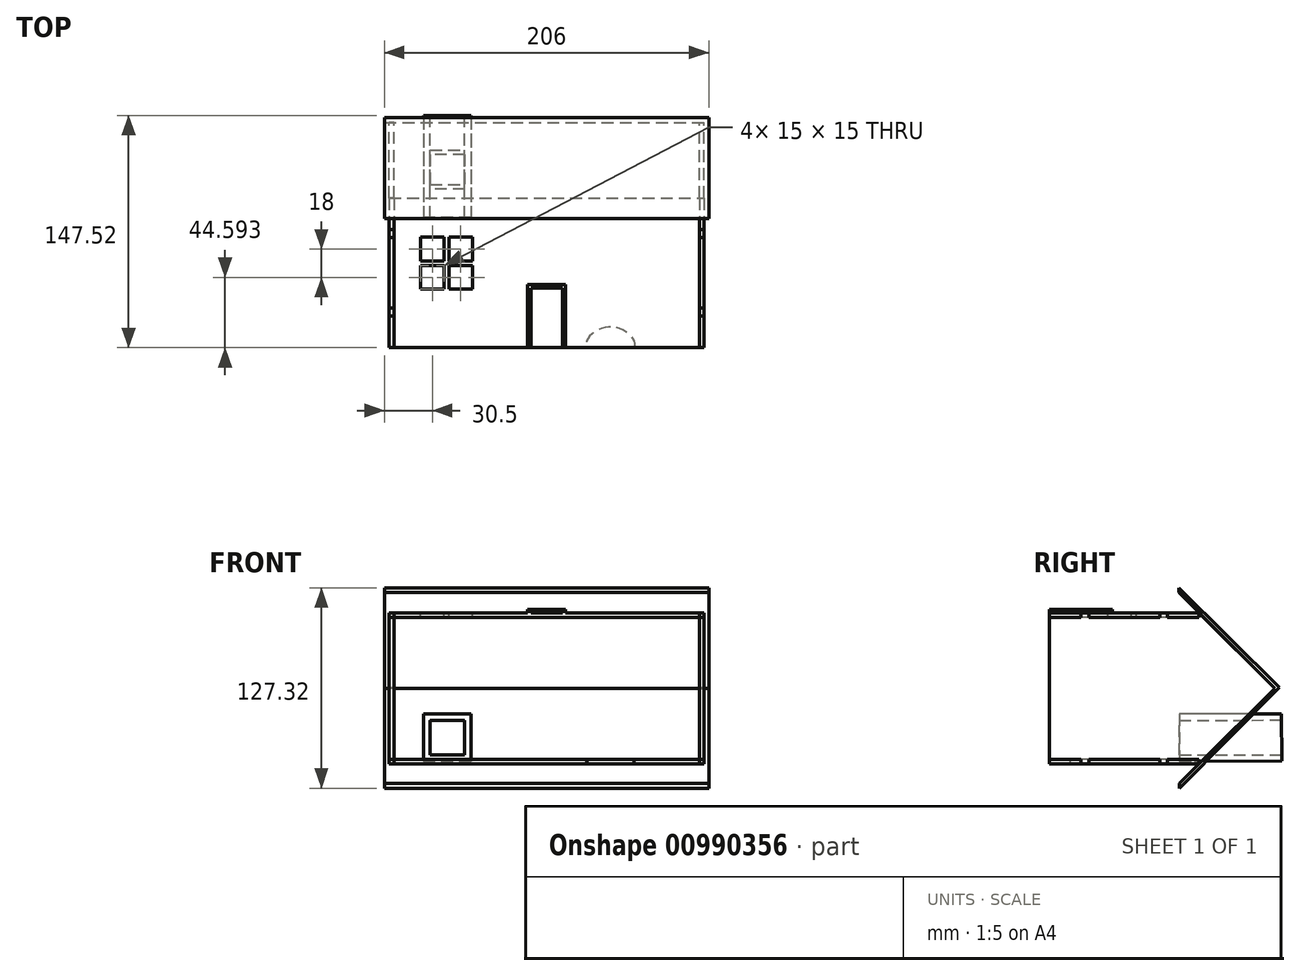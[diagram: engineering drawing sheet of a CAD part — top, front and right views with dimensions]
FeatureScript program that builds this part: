
annotation { "Feature Type Name" : "Feature", "Feature Type Description" : "" }
export const myFeature = defineFeature(function(context is Context, id is Id, definition is map)
    precondition{}
    {
        {
            var Q0;
            Q0=qCreatedBy(makeId("Top.planeOp"),FACE);
            var sketch = newSketch(context, id + "F0", { "sketchPlane" : qUnion([Q0])});
            skLineSegment(sketch, "E0.bottom", {"start": v(-100, 95) * mm, "end": v(100, 95) * mm});
            skLineSegment(sketch, "E0.top", {"start": v(-100, 0) * mm, "end": v(100, 0) * mm});
            skLineSegment(sketch, "E0.left", {"start": v(-100, 95) * mm, "end": v(-100, 0) * mm});
            skLineSegment(sketch, "E0.right", {"start": v(100, 95) * mm, "end": v(100, 0) * mm});
            skLineSegment(sketch, "E1.bottom", {"start": v(-100, 25) * mm, "end": v(-97, 25) * mm});
            skLineSegment(sketch, "E1.top", {"start": v(-100, 20) * mm, "end": v(-97, 20) * mm});
            skLineSegment(sketch, "E1.left", {"start": v(-100, 25) * mm, "end": v(-100, 20) * mm});
            skLineSegment(sketch, "E1.right", {"start": v(-97, 25) * mm, "end": v(-97, 20) * mm});
            skLineSegment(sketch, "E2.bottom", {"start": v(-100, 75) * mm, "end": v(-97, 75) * mm});
            skLineSegment(sketch, "E2.top", {"start": v(-100, 70) * mm, "end": v(-97, 70) * mm});
            skLineSegment(sketch, "E2.left", {"start": v(-100, 75) * mm, "end": v(-100, 70) * mm});
            skLineSegment(sketch, "E2.right", {"start": v(-97, 75) * mm, "end": v(-97, 70) * mm});
            skLineSegment(sketch, "E3.bottom", {"start": v(97, 25) * mm, "end": v(100, 25) * mm});
            skLineSegment(sketch, "E3.top", {"start": v(97, 20) * mm, "end": v(100, 20) * mm});
            skLineSegment(sketch, "E3.left", {"start": v(97, 25) * mm, "end": v(97, 20) * mm});
            skLineSegment(sketch, "E3.right", {"start": v(100, 25) * mm, "end": v(100, 20) * mm});
            skLineSegment(sketch, "E4.bottom", {"start": v(97, 75) * mm, "end": v(100, 75) * mm});
            skLineSegment(sketch, "E4.top", {"start": v(97, 70) * mm, "end": v(100, 70) * mm});
            skLineSegment(sketch, "E4.left", {"start": v(97, 75) * mm, "end": v(97, 70) * mm});
            skLineSegment(sketch, "E4.right", {"start": v(100, 75) * mm, "end": v(100, 70) * mm});
            skSolve(sketch);
        }
        {
            var Q0;
            Q0 = qSketchRegion(id + "F0", true);
            extrude(context, id + "F1", {"entities" : qUnion([Q0]), "depth" : 3 * mm, "offsetDistance" : 25 * mm});
        }
        {
            var Q0;
            Q0=makeQuery(id+"F1.opExtrude","CAP_FACE",FACE,{"disambiguationData":[OSD([sQuery(id+"F0.wireOp",EDGE,"E0.bottom"),sQuery(id+"F0.wireOp",EDGE,"E0.top"),sQuery(id+"F0.wireOp",EDGE,"E0.left"),sQuery(id+"F0.wireOp",EDGE,"E0.right"),sQuery(id+"F0.wireOp",EDGE,"E1.left"),sQuery(id+"F0.wireOp",EDGE,"E2.left"),sQuery(id+"F0.wireOp",EDGE,"E3.right"),sQuery(id+"F0.wireOp",EDGE,"E4.right")])],"isStart":false});
            var sketch = newSketch(context, id + "F2", { "sketchPlane" : qUnion([Q0])});
            skLineSegment(sketch, "E5.bottom", {"start": v(-100, 75) * mm, "end": v(-97, 75) * mm});
            skLineSegment(sketch, "E5.top", {"start": v(-100, 70) * mm, "end": v(-97, 70) * mm});
            skLineSegment(sketch, "E5.left", {"start": v(-100, 75) * mm, "end": v(-100, 70) * mm});
            skLineSegment(sketch, "E5.right", {"start": v(-97, 75) * mm, "end": v(-97, 70) * mm});
            skLineSegment(sketch, "E6.bottom", {"start": v(-100, 25) * mm, "end": v(-97, 25) * mm});
            skLineSegment(sketch, "E6.top", {"start": v(-100, 20) * mm, "end": v(-97, 20) * mm});
            skLineSegment(sketch, "E6.left", {"start": v(-100, 25) * mm, "end": v(-100, 20) * mm});
            skLineSegment(sketch, "E6.right", {"start": v(-97, 25) * mm, "end": v(-97, 20) * mm});
            skLineSegment(sketch, "E7.bottom", {"start": v(97, 75) * mm, "end": v(100, 75) * mm});
            skLineSegment(sketch, "E7.top", {"start": v(97, 70) * mm, "end": v(100, 70) * mm});
            skLineSegment(sketch, "E7.left", {"start": v(97, 75) * mm, "end": v(97, 70) * mm});
            skLineSegment(sketch, "E7.right", {"start": v(100, 75) * mm, "end": v(100, 70) * mm});
            skLineSegment(sketch, "E8.bottom", {"start": v(97, 25) * mm, "end": v(100, 25) * mm});
            skLineSegment(sketch, "E8.top", {"start": v(97, 20) * mm, "end": v(100, 20) * mm});
            skLineSegment(sketch, "E8.left", {"start": v(97, 25) * mm, "end": v(97, 20) * mm});
            skLineSegment(sketch, "E8.right", {"start": v(100, 25) * mm, "end": v(100, 20) * mm});
            skSolve(sketch);
        }
        {
            var Q0;
            Q0 = qSketchRegion(id + "F2", true);
            extrude(context, id + "F3", {"entities" : qUnion([Q0]), "operationType" : NewBodyOperationType.REMOVE, "oppositeDirection" : true, "depth" : 3 * mm, "offsetDistance" : 25 * mm});
        }
        {
            var Q0;
            Q0=makeQuery(id+"F1.opExtrude","CAP_FACE",FACE,{"disambiguationData":[OSD([sQuery(id+"F0.wireOp",EDGE,"E0.bottom"),sQuery(id+"F0.wireOp",EDGE,"E0.top"),sQuery(id+"F0.wireOp",EDGE,"E0.left"),sQuery(id+"F0.wireOp",EDGE,"E0.right"),sQuery(id+"F0.wireOp",EDGE,"E1.left"),sQuery(id+"F0.wireOp",EDGE,"E2.left"),sQuery(id+"F0.wireOp",EDGE,"E3.right"),sQuery(id+"F0.wireOp",EDGE,"E4.right")])],"isStart":true});
            cPlane(context, id + "F4", {"entities" : qUnion([Q0]), "cplaneType" : CPlaneType.OFFSET, "offset" : 45 * mm, "width" : 150 * mm, "height" : 150 * mm});
        }
        {
            var Q0;
            Q0=makeQuery(id+"F1.opExtrude","SWEPT_BODY",BODY,{"disambiguationData":[OSD([sQuery(id+"F0.wireOp",EDGE,"E0.bottom"),sQuery(id+"F0.wireOp",EDGE,"E0.top"),sQuery(id+"F0.wireOp",EDGE,"E0.left"),sQuery(id+"F0.wireOp",EDGE,"E0.right"),sQuery(id+"F0.wireOp",EDGE,"E1.left"),sQuery(id+"F0.wireOp",EDGE,"E2.left"),sQuery(id+"F0.wireOp",EDGE,"E3.right"),sQuery(id+"F0.wireOp",EDGE,"E4.right")])]});
            var Q1;
            Q1=qCreatedBy(id+"F4.planeOp",FACE);
            mirror(context, id + "F5", {"entities" : qUnion([Q0]), "mirrorPlane" : qUnion([Q1])});
        }
        {
            var Q0;
            Q0=qCreatedBy(makeId("Right.planeOp"),FACE);
            cPlane(context, id + "F6", {"entities" : qUnion([Q0]), "cplaneType" : CPlaneType.OFFSET, "offset" : 100 * mm, "width" : 150 * mm, "height" : 150 * mm});
        }
        {
            var Q0;
            Q0=qCreatedBy(id+"F6.planeOp",FACE);
            var sketch = newSketch(context, id + "F7", { "sketchPlane" : qUnion([Q0])});
            skLineSegment(sketch, "E9.bottom", {"start": v(95, 3) * mm, "end": v(0, 3) * mm});
            skLineSegment(sketch, "E9.top", {"start": v(95, -93) * mm, "end": v(0, -93) * mm});
            skLineSegment(sketch, "E9.left", {"start": v(95, 3) * mm, "end": v(95, -93) * mm});
            skLineSegment(sketch, "E9.right", {"start": v(0, 3) * mm, "end": v(0, -93) * mm});
            skLineSegment(sketch, "E10", {"start": v(95, 3) * mm, "end": v(143, -45) * mm});
            skLineSegment(sketch, "E11", {"start": v(143, -45) * mm, "end": v(95, -93) * mm});
            skLineSegment(sketch, "E12.bottom", {"start": v(95, -93) * mm, "end": v(75, -93) * mm});
            skLineSegment(sketch, "E12.top", {"start": v(95, -90) * mm, "end": v(75, -90) * mm});
            skLineSegment(sketch, "E12.left", {"start": v(95, -93) * mm, "end": v(95, -90) * mm});
            skLineSegment(sketch, "E12.right", {"start": v(75, -93) * mm, "end": v(75, -90) * mm});
            skLineSegment(sketch, "E13.bottom", {"start": v(95, 3) * mm, "end": v(82.7, 3) * mm});
            skLineSegment(sketch, "E13.top", {"start": v(95, 0) * mm, "end": v(82.7, 0) * mm});
            skLineSegment(sketch, "E13.left", {"start": v(95, 3) * mm, "end": v(95, 0) * mm});
            skLineSegment(sketch, "E13.right", {"start": v(82.7, 3) * mm, "end": v(82.7, 0) * mm});
            skLineSegment(sketch, "E14.bottom", {"start": v(0, 3) * mm, "end": v(20, 3) * mm});
            skLineSegment(sketch, "E14.top", {"start": v(0, 0) * mm, "end": v(20, 0) * mm});
            skLineSegment(sketch, "E14.left", {"start": v(0, 3) * mm, "end": v(0, 0) * mm});
            skLineSegment(sketch, "E14.right", {"start": v(20, 3) * mm, "end": v(20, 0) * mm});
            skLineSegment(sketch, "E15.bottom", {"start": v(0, -93) * mm, "end": v(20, -93) * mm});
            skLineSegment(sketch, "E15.top", {"start": v(0, -90) * mm, "end": v(20, -90) * mm});
            skLineSegment(sketch, "E15.left", {"start": v(0, -93) * mm, "end": v(0, -90) * mm});
            skLineSegment(sketch, "E15.right", {"start": v(20, -93) * mm, "end": v(20, -90) * mm});
            skPoint(sketch, "E16.oppositeSnap0", {"position": v(47.5, 3) * mm});
            skLineSegment(sketch, "E16.bottom", {"start": v(60.82, 3) * mm, "end": v(47.5, 3) * mm});
            skLineSegment(sketch, "E16.top", {"start": v(60.82, 0) * mm, "end": v(47.5, 0) * mm});
            skLineSegment(sketch, "E16.left", {"start": v(60.82, 3) * mm, "end": v(60.82, 0) * mm});
            skLineSegment(sketch, "E16.right", {"start": v(47.5, 3) * mm, "end": v(47.5, 0) * mm});
            skLineSegment(sketch, "E17.bottom", {"start": v(61.42, -93) * mm, "end": v(47.08, -93) * mm});
            skLineSegment(sketch, "E17.top", {"start": v(61.42, -72.68) * mm, "end": v(47.08, -72.68) * mm});
            skLineSegment(sketch, "E17.left", {"start": v(61.42, -93) * mm, "end": v(61.42, -72.68) * mm});
            skLineSegment(sketch, "E17.right", {"start": v(47.08, -93) * mm, "end": v(47.08, -72.68) * mm});
            skSolve(sketch);
        }
        {
            var Q0;
            Q0 = qSketchRegion(id + "F7", true);
            extrude(context, id + "F8", {"entities" : qUnion([Q0]), "oppositeDirection" : true, "depth" : 3 * mm, "offsetDistance" : 25 * mm});
        }
        {
            var Q0;
            Q0=makeQuery(id+"F8.opExtrude","SWEPT_BODY",BODY,{"disambiguationData":[OSD([sQuery(id+"F7.wireOp",EDGE,"E9.bottom"),sQuery(id+"F7.wireOp",EDGE,"E9.top"),sQuery(id+"F7.wireOp",EDGE,"E9.right"),sQuery(id+"F7.wireOp",EDGE,"E10"),sQuery(id+"F7.wireOp",EDGE,"E11"),sQuery(id+"F7.wireOp",EDGE,"E12.bottom"),sQuery(id+"F7.wireOp",EDGE,"E13.bottom"),sQuery(id+"F7.wireOp",EDGE,"E14.bottom"),sQuery(id+"F7.wireOp",EDGE,"E14.left"),sQuery(id+"F7.wireOp",EDGE,"E15.bottom"),sQuery(id+"F7.wireOp",EDGE,"E15.left"),sQuery(id+"F7.wireOp",EDGE,"E16.bottom"),sQuery(id+"F7.wireOp",EDGE,"E17.bottom")])]});
            var Q1;
            Q1=qCreatedBy(makeId("Right.planeOp"),FACE);
            mirror(context, id + "F9", {"entities" : qUnion([Q0]), "mirrorPlane" : qUnion([Q1])});
        }
        {
            var Q0;
            Q0=makeQuery(id+"F8.opExtrude","CAP_FACE",FACE,{"disambiguationData":[OSD([sQuery(id+"F7.wireOp",EDGE,"E9.bottom"),sQuery(id+"F7.wireOp",EDGE,"E9.top"),sQuery(id+"F7.wireOp",EDGE,"E9.right"),sQuery(id+"F7.wireOp",EDGE,"E10"),sQuery(id+"F7.wireOp",EDGE,"E11"),sQuery(id+"F7.wireOp",EDGE,"E12.bottom"),sQuery(id+"F7.wireOp",EDGE,"E13.bottom"),sQuery(id+"F7.wireOp",EDGE,"E14.bottom"),sQuery(id+"F7.wireOp",EDGE,"E14.left"),sQuery(id+"F7.wireOp",EDGE,"E15.bottom"),sQuery(id+"F7.wireOp",EDGE,"E15.left"),sQuery(id+"F7.wireOp",EDGE,"E16.bottom"),sQuery(id+"F7.wireOp",EDGE,"E17.bottom")])],"isStart":true});
            cPlane(context, id + "F10", {"entities" : qUnion([Q0]), "cplaneType" : CPlaneType.OFFSET, "offset" : 3 * mm, "width" : 150 * mm, "height" : 150 * mm});
        }
        {
            var Q0;
            Q0=qCreatedBy(id+"F10.planeOp",FACE);
            var sketch = newSketch(context, id + "F11", { "sketchPlane" : qUnion([Q0])});
            skLineSegment(sketch, "E18", {"start": v(82.1, 18.9) * mm, "end": v(82.1, 15.9) * mm});
            skLineSegment(sketch, "E19", {"start": v(82.1, 15.9) * mm, "end": v(143, -45) * mm});
            skLineSegment(sketch, "E20", {"start": v(143, -45) * mm, "end": v(82.59, -105.41) * mm});
            skLineSegment(sketch, "E21", {"start": v(82.59, -105.41) * mm, "end": v(82.59, -108.41) * mm});
            skLineSegment(sketch, "E22", {"start": v(82.59, -108.41) * mm, "end": v(145.96, -44.5) * mm});
            skLineSegment(sketch, "E23", {"start": v(145.96, -44.5) * mm, "end": v(82.1, 18.9) * mm});
            skSolve(sketch);
        }
        {
            var Q0;
            Q0 = qSketchRegion(id + "F11", true);
            extrude(context, id + "F12", {"entities" : qUnion([Q0]), "oppositeDirection" : true, "depth" : 206 * mm, "offsetDistance" : 25 * mm});
        }
        {
            var Q0;
            Q0=makeQuery(id+"F1.opExtrude","CAP_FACE",FACE,{"disambiguationData":[OSD([sQuery(id+"F0.wireOp",EDGE,"E0.bottom"),sQuery(id+"F0.wireOp",EDGE,"E0.top"),sQuery(id+"F0.wireOp",EDGE,"E0.left"),sQuery(id+"F0.wireOp",EDGE,"E0.right"),sQuery(id+"F0.wireOp",EDGE,"E1.left"),sQuery(id+"F0.wireOp",EDGE,"E2.left"),sQuery(id+"F0.wireOp",EDGE,"E3.right"),sQuery(id+"F0.wireOp",EDGE,"E4.right")])],"isStart":false});
            var sketch = newSketch(context, id + "F13", { "sketchPlane" : qUnion([Q0])});
            skLineSegment(sketch, "E24.bottom", {"start": v(-80, 70.1) * mm, "end": v(-65, 70.1) * mm});
            skLineSegment(sketch, "E24.top", {"start": v(-80, 55.1) * mm, "end": v(-65, 55.1) * mm});
            skLineSegment(sketch, "E24.left", {"start": v(-80, 70.1) * mm, "end": v(-80, 55.1) * mm});
            skLineSegment(sketch, "E24.right", {"start": v(-65, 70.1) * mm, "end": v(-65, 55.1) * mm});
            skLineSegment(sketch, "E25.bottom", {"start": v(-62, 70.1) * mm, "end": v(-47, 70.1) * mm});
            skLineSegment(sketch, "E25.top", {"start": v(-62, 55.1) * mm, "end": v(-47, 55.1) * mm});
            skLineSegment(sketch, "E25.left", {"start": v(-62, 70.1) * mm, "end": v(-62, 55.1) * mm});
            skLineSegment(sketch, "E25.right", {"start": v(-47, 70.1) * mm, "end": v(-47, 55.1) * mm});
            skLineSegment(sketch, "E26.bottom", {"start": v(-62, 52.1) * mm, "end": v(-47, 52.1) * mm});
            skLineSegment(sketch, "E26.top", {"start": v(-62, 37.1) * mm, "end": v(-47, 37.1) * mm});
            skLineSegment(sketch, "E26.left", {"start": v(-62, 52.1) * mm, "end": v(-62, 37.1) * mm});
            skLineSegment(sketch, "E26.right", {"start": v(-47, 52.1) * mm, "end": v(-47, 37.1) * mm});
            skLineSegment(sketch, "E27.bottom", {"start": v(-80, 52.1) * mm, "end": v(-65, 52.1) * mm});
            skLineSegment(sketch, "E27.top", {"start": v(-80, 37.1) * mm, "end": v(-65, 37.1) * mm});
            skLineSegment(sketch, "E27.left", {"start": v(-80, 52.1) * mm, "end": v(-80, 37.1) * mm});
            skLineSegment(sketch, "E27.right", {"start": v(-65, 52.1) * mm, "end": v(-65, 37.1) * mm});
            skSolve(sketch);
        }
        {
            var Q0;
            Q0 = qSketchRegion(id + "F13", true);
            extrude(context, id + "F14", {"entities" : qUnion([Q0]), "operationType" : NewBodyOperationType.REMOVE, "oppositeDirection" : true, "depth" : 5 * mm, "offsetDistance" : 25 * mm});
        }
        {
            var Q0;
            Q0=makeQuery(id+"F13.imprint","IMPRINT",FACE,{"disambiguationData":[TD([[makeQuery(id+"F13.imprint","IMPRINT",EDGE,{"derivedFrom":sQuery(id+"F13.wireOp",EDGE,"E24.bottom")}),1.0]])]});
            var sketch = newSketch(context, id + "F15", { "sketchPlane" : qUnion([Q0])});
            skLineSegment(sketch, "E28.bottom", {"start": v(-12, 40) * mm, "end": v(12, 40) * mm});
            skLineSegment(sketch, "E28.top", {"start": v(-12, 0) * mm, "end": v(12, 0) * mm});
            skLineSegment(sketch, "E28.left", {"start": v(-12, 40) * mm, "end": v(-12, 0) * mm});
            skLineSegment(sketch, "E28.right", {"start": v(12, 40) * mm, "end": v(12, 0) * mm});
            skSolve(sketch);
        }
        {
            var Q0;
            Q0 = qSketchRegion(id + "F15", true);
            extrude(context, id + "F16", {"entities" : qUnion([Q0]), "operationType" : NewBodyOperationType.ADD, "depth" : 2 * mm, "offsetDistance" : 25 * mm});
        }
        {
            var Q0;
            Q0=makeQuery(id+"F16.opExtrude","CAP_FACE",FACE,{"disambiguationData":[OSD([sQuery(id+"F15.wireOp",EDGE,"E28.bottom"),sQuery(id+"F15.wireOp",EDGE,"E28.top"),sQuery(id+"F15.wireOp",EDGE,"E28.left"),sQuery(id+"F15.wireOp",EDGE,"E28.right")])],"isStart":false});
            var sketch = newSketch(context, id + "F17", { "sketchPlane" : qUnion([Q0])});
            skLineSegment(sketch, "E29.bottom", {"start": v(-10, 38) * mm, "end": v(10, 38) * mm});
            skLineSegment(sketch, "E29.top", {"start": v(-10, 0) * mm, "end": v(10, 0) * mm});
            skLineSegment(sketch, "E29.left", {"start": v(-10, 38) * mm, "end": v(-10, 0) * mm});
            skLineSegment(sketch, "E29.right", {"start": v(10, 38) * mm, "end": v(10, 0) * mm});
            skSolve(sketch);
        }
        {
            var Q0;
            Q0 = qSketchRegion(id + "F17", true);
            extrude(context, id + "F18", {"entities" : qUnion([Q0]), "operationType" : NewBodyOperationType.REMOVE, "oppositeDirection" : true, "depth" : 2 * mm, "offsetDistance" : 25 * mm});
        }
        {
            var Q0;
            Q0=makeQuery(id+"F12.opExtrude","CAP_VERTEX",VERTEX,{"disambiguationData":[OSD([sQuery(id+"F11.wireOp",EDGE,"E18"),sQuery(id+"F11.wireOp",EDGE,"E23")])],"isStart":false});
            var Q1;
            Q1=makeQuery(id+"F12.opExtrude","CAP_VERTEX",VERTEX,{"disambiguationData":[OSD([sQuery(id+"F11.wireOp",EDGE,"E21"),sQuery(id+"F11.wireOp",EDGE,"E22")])],"isStart":false});
            var Q2;
            Q2=makeQuery(id+"F12.opExtrude","CAP_VERTEX",VERTEX,{"disambiguationData":[OSD([sQuery(id+"F11.wireOp",EDGE,"E21"),sQuery(id+"F11.wireOp",EDGE,"E22")])],"isStart":true});
            cPlane(context, id + "F19", {"entities" : qUnion([Q0, Q1, Q2]), "cplaneType" : CPlaneType.THREE_POINT, "offset" : 25 * mm, "width" : 150 * mm, "height" : 150 * mm});
        }
        {
            var Q0;
            Q0=qCreatedBy(id+"F19.planeOp",FACE);
            var sketch = newSketch(context, id + "F20", { "sketchPlane" : qUnion([Q0])});
            skLineSegment(sketch, "E30.bottom", {"start": v(48, -61.73) * mm, "end": v(78, -61.73) * mm});
            skLineSegment(sketch, "E30.top", {"start": v(48, -91.73) * mm, "end": v(78, -91.73) * mm});
            skLineSegment(sketch, "E30.left", {"start": v(48, -61.73) * mm, "end": v(48, -91.73) * mm});
            skLineSegment(sketch, "E30.right", {"start": v(78, -61.73) * mm, "end": v(78, -91.73) * mm});
            skSolve(sketch);
        }
        {
            var Q0;
            Q0 = qSketchRegion(id + "F20", true);
            extrude(context, id + "F21", {"entities" : qUnion([Q0]), "depth" : 65 * mm, "offsetDistance" : 25 * mm});
        }
        {
            var Q0;
            Q0=makeQuery(id+"F21.opExtrude","CAP_FACE",FACE,{"disambiguationData":[OSD([sQuery(id+"F20.wireOp",EDGE,"E30.bottom"),sQuery(id+"F20.wireOp",EDGE,"E30.top"),sQuery(id+"F20.wireOp",EDGE,"E30.left"),sQuery(id+"F20.wireOp",EDGE,"E30.right")])],"isStart":false});
            var sketch = newSketch(context, id + "F22", { "sketchPlane" : qUnion([Q0])});
            skLineSegment(sketch, "E31.bottom", {"start": v(74, -87.73) * mm, "end": v(52, -87.73) * mm});
            skLineSegment(sketch, "E31.top", {"start": v(74, -65.73) * mm, "end": v(52, -65.73) * mm});
            skLineSegment(sketch, "E31.left", {"start": v(74, -87.73) * mm, "end": v(74, -65.73) * mm});
            skLineSegment(sketch, "E31.right", {"start": v(52, -87.73) * mm, "end": v(52, -65.73) * mm});
            skSolve(sketch);
        }
        {
            var Q0;
            Q0 = qSketchRegion(id + "F22", true);
            extrude(context, id + "F23", {"entities" : qUnion([Q0]), "operationType" : NewBodyOperationType.REMOVE, "endBound" : BoundingType.THROUGH_ALL, "oppositeDirection" : true, "depth" : 80 * mm, "offsetDistance" : 25 * mm});
        }
        {
            var Q0;
            Q0=makeQuery(id+"F5.opPattern","COPY",FACE,{"derivedFrom":makeQuery(id+"F1.opExtrude","CAP_FACE",FACE,{"disambiguationData":[OSD([sQuery(id+"F0.wireOp",EDGE,"E0.bottom"),sQuery(id+"F0.wireOp",EDGE,"E0.top"),sQuery(id+"F0.wireOp",EDGE,"E0.left"),sQuery(id+"F0.wireOp",EDGE,"E0.right"),sQuery(id+"F0.wireOp",EDGE,"E1.left"),sQuery(id+"F0.wireOp",EDGE,"E2.left"),sQuery(id+"F0.wireOp",EDGE,"E3.right"),sQuery(id+"F0.wireOp",EDGE,"E4.right")])],"isStart":false}),"instanceName":"1"});
            var sketch = newSketch(context, id + "F24", { "sketchPlane" : qUnion([Q0])});
            skFitSpline(sketch, "E32", {"points": [v(55.58, 0) * mm, v(40.58, -13.23) * mm, v(25.58, 0) * mm, v(55.58, 0) * mm]});
            skSolve(sketch);
        }
        {
            var Q0;
            Q0 = qSketchRegion(id + "F24", true);
            extrude(context, id + "F25", {"entities" : qUnion([Q0]), "operationType" : NewBodyOperationType.REMOVE, "oppositeDirection" : true, "depth" : 25 * mm, "offsetDistance" : 25 * mm});
        }
    });
